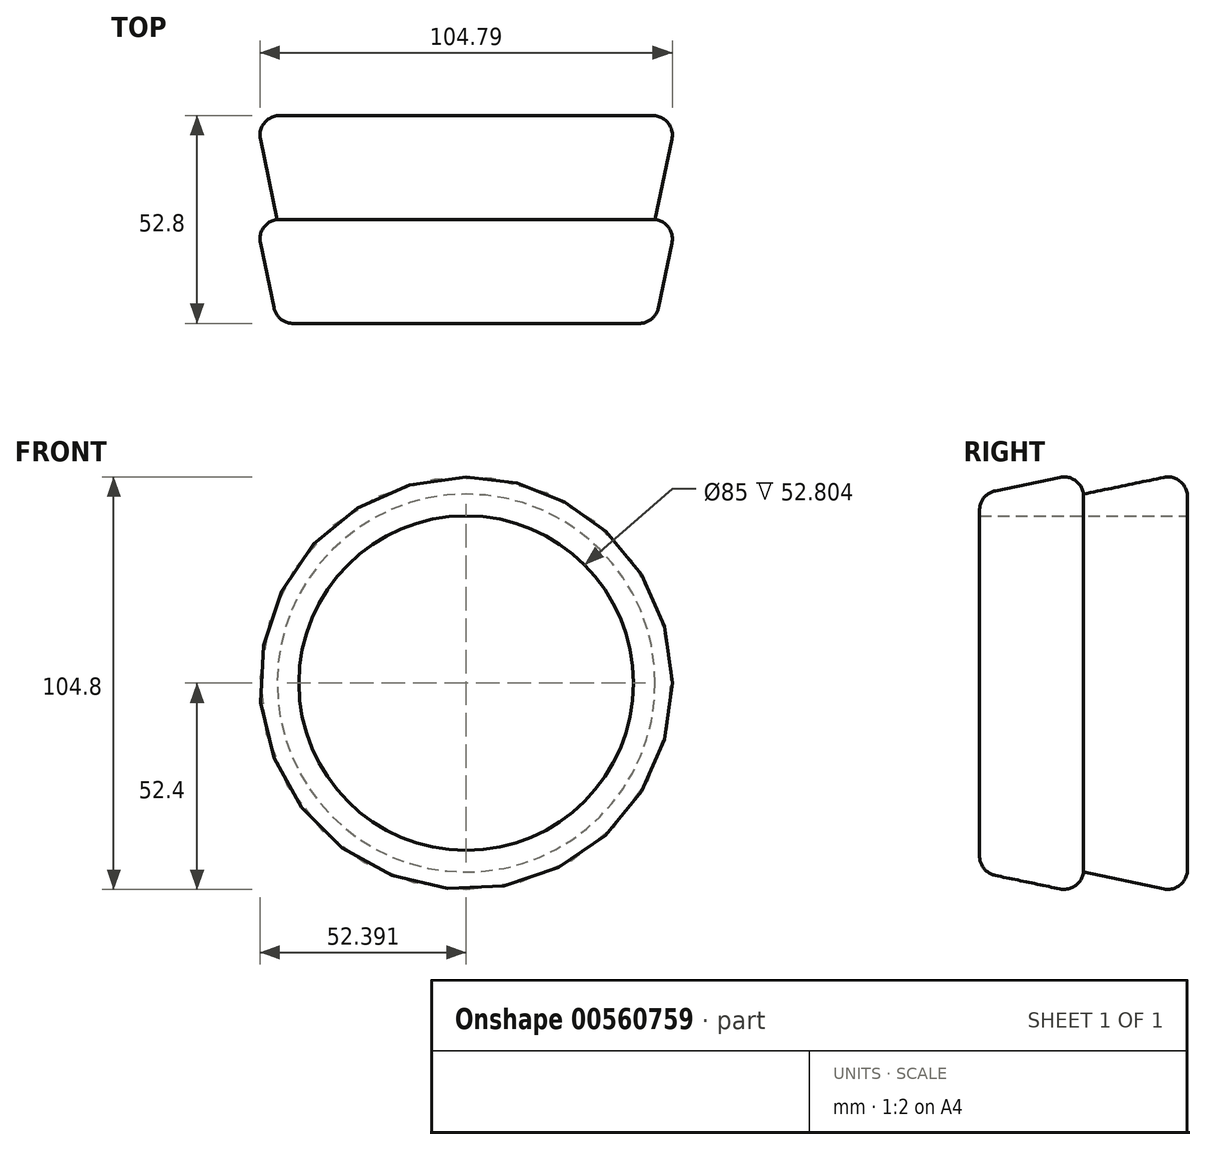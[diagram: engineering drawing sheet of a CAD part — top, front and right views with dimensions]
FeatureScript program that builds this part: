
annotation { "Feature Type Name" : "Feature", "Feature Type Description" : "" }
export const myFeature = defineFeature(function(context is Context, id is Id, definition is map)
    precondition{}
    {
        {
            var Q0;
            Q0=qCreatedBy(makeId("Top.planeOp"),FACE);
            var sketch = newSketch(context, id + "F0", { "sketchPlane" : qUnion([Q0])});
            skLineSegment(sketch, "E0.bottom", {"start": v(53.54, 26.4) * mm, "end": v(11.04, 26.4) * mm});
            skLineSegment(sketch, "E0.top", {"start": v(53.54, -26.4) * mm, "end": v(11.04, -26.4) * mm});
            skLineSegment(sketch, "E0.left", {"start": v(53.54, 26.4) * mm, "end": v(53.54, -26.4) * mm});
            skLineSegment(sketch, "E0.right", {"start": v(11.04, 26.4) * mm, "end": v(11.04, -26.4) * mm});
            skPoint(sketch, "E0.middle", {"position": v(32.3, 0) * mm});
            skLineSegment(sketch, "E1", {"start": v(11.04, -26.4) * mm, "end": v(0, -26.4) * mm});
            skLineSegment(sketch, "E2", {"start": v(0, -26.4) * mm, "end": v(0, 26.4) * mm});
            skLineSegment(sketch, "E3", {"start": v(0, 26.4) * mm, "end": v(11.04, 26.4) * mm});
            skLineSegment(sketch, "E4", {"start": v(5.52, 26.4) * mm, "end": v(5.52, -26.4) * mm});
            skLineSegment(sketch, "E5", {"start": v(5.52, -26.4) * mm, "end": v(0, 0) * mm});
            skLineSegment(sketch, "E6", {"start": v(0, 0) * mm, "end": v(5.52, 0) * mm});
            skLineSegment(sketch, "E7", {"start": v(5.52, 0) * mm, "end": v(0, 26.4) * mm});
            skSolve(sketch);
        }
        {
            var Q0;
            Q0=makeQuery(id+"F0.imprint","IMPRINT",FACE,{"disambiguationData":[TD([[makeQuery(id+"F0.imprint","IMPRINT",EDGE,{"derivedFrom":sQuery(id+"F0.wireOp",EDGE,"E0.right")}),-1.0]])]});
            var Q1;
            {var subQ0=sQuery(id+"F0.wireOp",EDGE,"E5");Q1=makeQuery(id+"F0.imprint","IMPRINT",FACE,{"disambiguationData":[TD([[makeQuery(id+"F0.imprint","IMPRINT",EDGE,{"derivedFrom":subQ0}),-1.0]])]});}
            var Q2;
            {var subQ0=sQuery(id+"F0.wireOp",EDGE,"E7");Q2=makeQuery(id+"F0.imprint","IMPRINT",FACE,{"disambiguationData":[TD([[makeQuery(id+"F0.imprint","IMPRINT",EDGE,{"derivedFrom":subQ0}),-1.0]])]});}
            var Q3;
            Q3=sQuery(id+"F0.wireOp",EDGE,"E0.left");
            revolve(context, id + "F1", {"entities" : qUnion([Q0, Q1, Q2]), "axis" : qUnion([Q3]), "revolveType" : RevolveType.FULL});
        }
        {
            var Q0;
            Q0=makeQuery(id+"F1.opRevolve","SWEPT_EDGE",EDGE,{"disambiguationData":[OSD([sQuery(id+"F0.wireOp",EDGE,"E2"),sQuery(id+"F0.wireOp",EDGE,"E3"),sQuery(id+"F0.wireOp",EDGE,"E7")])]});
            var Q1;
            Q1=makeQuery(id+"F1.opRevolve","SWEPT_EDGE",EDGE,{"disambiguationData":[OSD([sQuery(id+"F0.wireOp",EDGE,"E2"),sQuery(id+"F0.wireOp",EDGE,"E5"),sQuery(id+"F0.wireOp",EDGE,"E6")])]});
            var Q2;
            Q2=makeQuery(id+"F1.opRevolve","SWEPT_EDGE",EDGE,{"disambiguationData":[OSD([sQuery(id+"F0.wireOp",EDGE,"E1"),sQuery(id+"F0.wireOp",EDGE,"E4"),sQuery(id+"F0.wireOp",EDGE,"E5")])]});
            fillet(context, id + "F2", {"entities" : qUnion([Q0, Q1, Q2]), "radius" : 5 * mm, "tangentPropagation" : true, "allowEdgeOverflow" : false});
        }
    });
